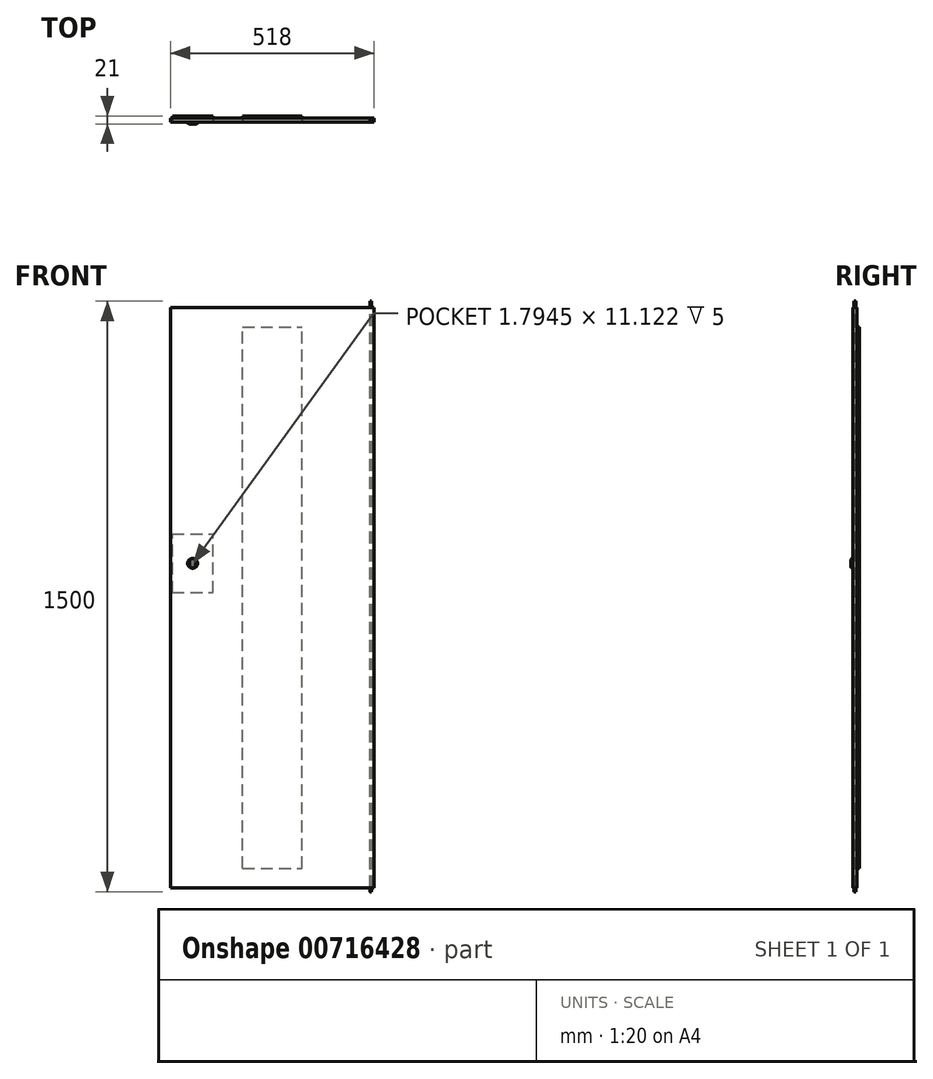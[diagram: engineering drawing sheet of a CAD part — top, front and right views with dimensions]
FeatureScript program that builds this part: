
annotation { "Feature Type Name" : "Feature", "Feature Type Description" : "" }
export const myFeature = defineFeature(function(context is Context, id is Id, definition is map)
    precondition{}
    {
        {
            var Q0;
            Q0=qCreatedBy(makeId("Top.planeOp"),FACE);
            var sketch = newSketch(context, id + "F0", { "sketchPlane" : qUnion([Q0])});
            skLineSegment(sketch, "E0.bottom", {"start": v(0, 0) * mm, "end": v(518, 0) * mm});
            skLineSegment(sketch, "E0.top", {"start": v(0, 10) * mm, "end": v(518, 10) * mm});
            skLineSegment(sketch, "E0.left", {"start": v(0, 0) * mm, "end": v(0, 10) * mm});
            skLineSegment(sketch, "E0.right", {"start": v(518, 0) * mm, "end": v(518, 10) * mm});
            skSolve(sketch);
        }
        {
            var Q0;
            Q0=qSketchRegion(id+"F0",true);
            extrude(context, id + "F1", {"entities" : qUnion([Q0]), "depth" : 1474 * mm, "offsetDistance" : 25 * mm});
        }
        {
            var Q0;
            Q0=makeQuery(id+"F1.opExtrude","SWEPT_FACE",FACE,{"disambiguationData":[OSD([sQuery(id+"F0.wireOp",EDGE,"E0.top")])]});
            shell(context, id + "F2", {"entities" : qUnion([Q0]), "thickness" : 1 * mm});
        }
        {
            var Q0;
            Q0=makeQuery(id+"F1.opExtrude","CAP_FACE",FACE,{"disambiguationData":[OSD([sQuery(id+"F0.wireOp",EDGE,"E0.bottom"),sQuery(id+"F0.wireOp",EDGE,"E0.top"),sQuery(id+"F0.wireOp",EDGE,"E0.left"),sQuery(id+"F0.wireOp",EDGE,"E0.right")])],"isStart":true});
            var sketch = newSketch(context, id + "F3", { "sketchPlane" : qUnion([Q0])});
            skCircle(sketch, "E1", {"center": v(509, -5) * mm, "radius": 2 * mm});
            skPoint(sketch, "E1.centerSnap0", {"position": v(518, -5) * mm});
            skSolve(sketch);
        }
        {
            var Q0;
            Q0=qSketchRegion(id+"F3",true);
            extrude(context, id + "F4", {"entities" : qUnion([Q0]), "operationType" : NewBodyOperationType.ADD, "depth" : 10 * mm, "offsetDistance" : 25 * mm, "hasSecondDirection" : true, "secondDirectionOppositeDirection" : true, "secondDirectionDepth" : 1490 * mm});
        }
        {
            var Q0;
            Q0=makeQuery(id+"F1.opExtrude","SWEPT_FACE",FACE,{"disambiguationData":[OSD([sQuery(id+"F0.wireOp",EDGE,"E0.bottom")])]});
            var sketch = newSketch(context, id + "F5", { "sketchPlane" : qUnion([Q0])});
            skCircle(sketch, "E2", {"center": v(56.6, 824) * mm, "radius": 12.5 * mm});
            skSolve(sketch);
        }
        {
            var Q0;
            Q0 = qSketchRegion(id + "F5", true);
            extrude(context, id + "F6", {"entities" : qUnion([Q0]), "operationType" : NewBodyOperationType.ADD, "depth" : 5 * mm, "offsetDistance" : 25 * mm});
        }
        {
            var Q0;
            Q0=makeQuery(id+"F6.opExtrude","CAP_EDGE",EDGE,{"disambiguationData":[OSD([sQuery(id+"F5.wireOp",EDGE,"E2")])],"isStart":false});
            chamfer(context, id + "F7", {"entities" : qUnion([Q0]), "width" : 3 * mm, "tangentPropagation" : true});
        }
        {
            var Q0;
            Q0=makeQuery(id+"F6.opExtrude","CAP_FACE",FACE,{"disambiguationData":[OSD([sQuery(id+"F5.wireOp",EDGE,"E2")])],"isStart":false});
            var sketch = newSketch(context, id + "F8", { "sketchPlane" : qUnion([Q0])});
            skLineSegment(sketch, "E3.bottom", {"start": v(57.5, 829.56) * mm, "end": v(55.71, 829.56) * mm});
            skLineSegment(sketch, "E3.top", {"start": v(57.5, 818.44) * mm, "end": v(55.71, 818.44) * mm});
            skLineSegment(sketch, "E3.left", {"start": v(57.5, 829.56) * mm, "end": v(57.5, 818.44) * mm});
            skLineSegment(sketch, "E3.right", {"start": v(55.71, 829.56) * mm, "end": v(55.71, 818.44) * mm});
            skPoint(sketch, "E3.middle", {"position": v(56.6, 824) * mm});
            skSolve(sketch);
        }
        {
            var Q0;
            Q0 = qSketchRegion(id + "F8", true);
            extrude(context, id + "F9", {"entities" : qUnion([Q0]), "operationType" : NewBodyOperationType.REMOVE, "oppositeDirection" : true, "depth" : 5 * mm, "offsetDistance" : 25 * mm});
        }
        {
            var Q0;
            Q0=makeQuery(id+"F2.opShell","OFFSET_FACE",FACE,{"disambiguationData":[OSD([sQuery(id+"F0.wireOp",EDGE,"E0.bottom")])]});
            var sketch = newSketch(context, id + "F10", { "sketchPlane" : qUnion([Q0])});
            skLineSegment(sketch, "E4.bottom", {"start": v(-5.33, 749.76) * mm, "end": v(-108.1, 749.76) * mm});
            skLineSegment(sketch, "E4.top", {"start": v(-5.33, 898.77) * mm, "end": v(-108.1, 898.77) * mm});
            skLineSegment(sketch, "E4.left", {"start": v(-5.33, 749.76) * mm, "end": v(-5.33, 898.77) * mm});
            skLineSegment(sketch, "E4.right", {"start": v(-108.1, 749.76) * mm, "end": v(-108.1, 898.77) * mm});
            skPoint(sketch, "E4.middle", {"position": v(-56.72, 824.27) * mm});
            skSolve(sketch);
        }
        {
            var Q0;
            Q0 = qSketchRegion(id + "F10", true);
            extrude(context, id + "F11", {"entities" : qUnion([Q0]), "operationType" : NewBodyOperationType.ADD, "depth" : 15 * mm, "offsetDistance" : 25 * mm});
        }
        {
            var Q0;
            Q0=makeQuery(id+"F2.opShell","OFFSET_FACE",FACE,{"disambiguationData":[OSD([sQuery(id+"F0.wireOp",EDGE,"E0.bottom")])]});
            var sketch = newSketch(context, id + "F12", { "sketchPlane" : qUnion([Q0])});
            skLineSegment(sketch, "E5", {"start": v(-259, 1473) * mm, "end": v(-259, 0) * mm, "construction": true});
            skLineSegment(sketch, "E6.bottom", {"start": v(-184, 49) * mm, "end": v(-334, 49) * mm});
            skLineSegment(sketch, "E6.top", {"start": v(-184, 1424) * mm, "end": v(-334, 1424) * mm});
            skLineSegment(sketch, "E6.left", {"start": v(-184, 49) * mm, "end": v(-184, 1424) * mm});
            skLineSegment(sketch, "E6.right", {"start": v(-334, 49) * mm, "end": v(-334, 1424) * mm});
            skPoint(sketch, "E6.middle", {"position": v(-259, 736.5) * mm});
            skSolve(sketch);
        }
        {
            var Q0;
            Q0 = qSketchRegion(id + "F12", true);
            extrude(context, id + "F13", {"entities" : qUnion([Q0]), "operationType" : NewBodyOperationType.ADD, "depth" : 15 * mm, "offsetDistance" : 25 * mm});
        }
    });
